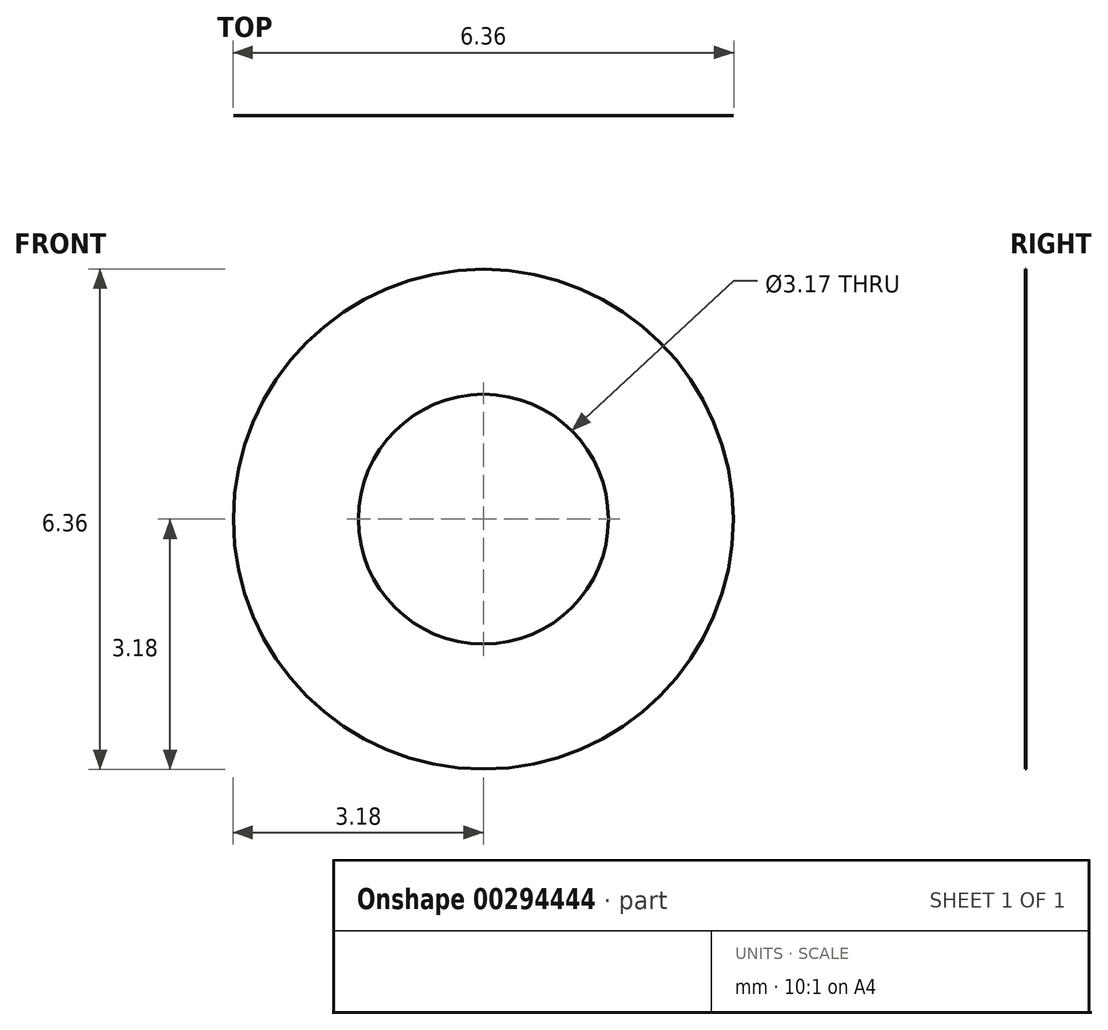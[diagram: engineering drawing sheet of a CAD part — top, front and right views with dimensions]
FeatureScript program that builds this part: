
annotation { "Feature Type Name" : "Feature", "Feature Type Description" : "" }
export const myFeature = defineFeature(function(context is Context, id is Id, definition is map)
    precondition{}
    {
        {
            var Q0;
            Q0=qCreatedBy(makeId("Front.planeOp"),FACE);
            var sketch = newSketch(context, id + "F0", { "sketchPlane" : qUnion([Q0])});
            skCircle(sketch, "E0", {"center": v(0, 0) * mm, "radius": 3.18 * mm});
            skCircle(sketch, "E1", {"center": v(0, 0) * mm, "radius": 1.59 * mm});
            skSolve(sketch);
        }
        {
            var Q0;
            Q0=makeQuery(id+"F0.imprint","IMPRINT",FACE,{"disambiguationData":[TD([[makeQuery(id+"F0.imprint","IMPRINT",EDGE,{"derivedFrom":sQuery(id+"F0.wireOp",EDGE,"E0")}),1.0]])]});
            extrude(context, id + "F1", {"entities" : qUnion([Q0]), "depth" : 1 / 203.2 * mm});
        }
    });
